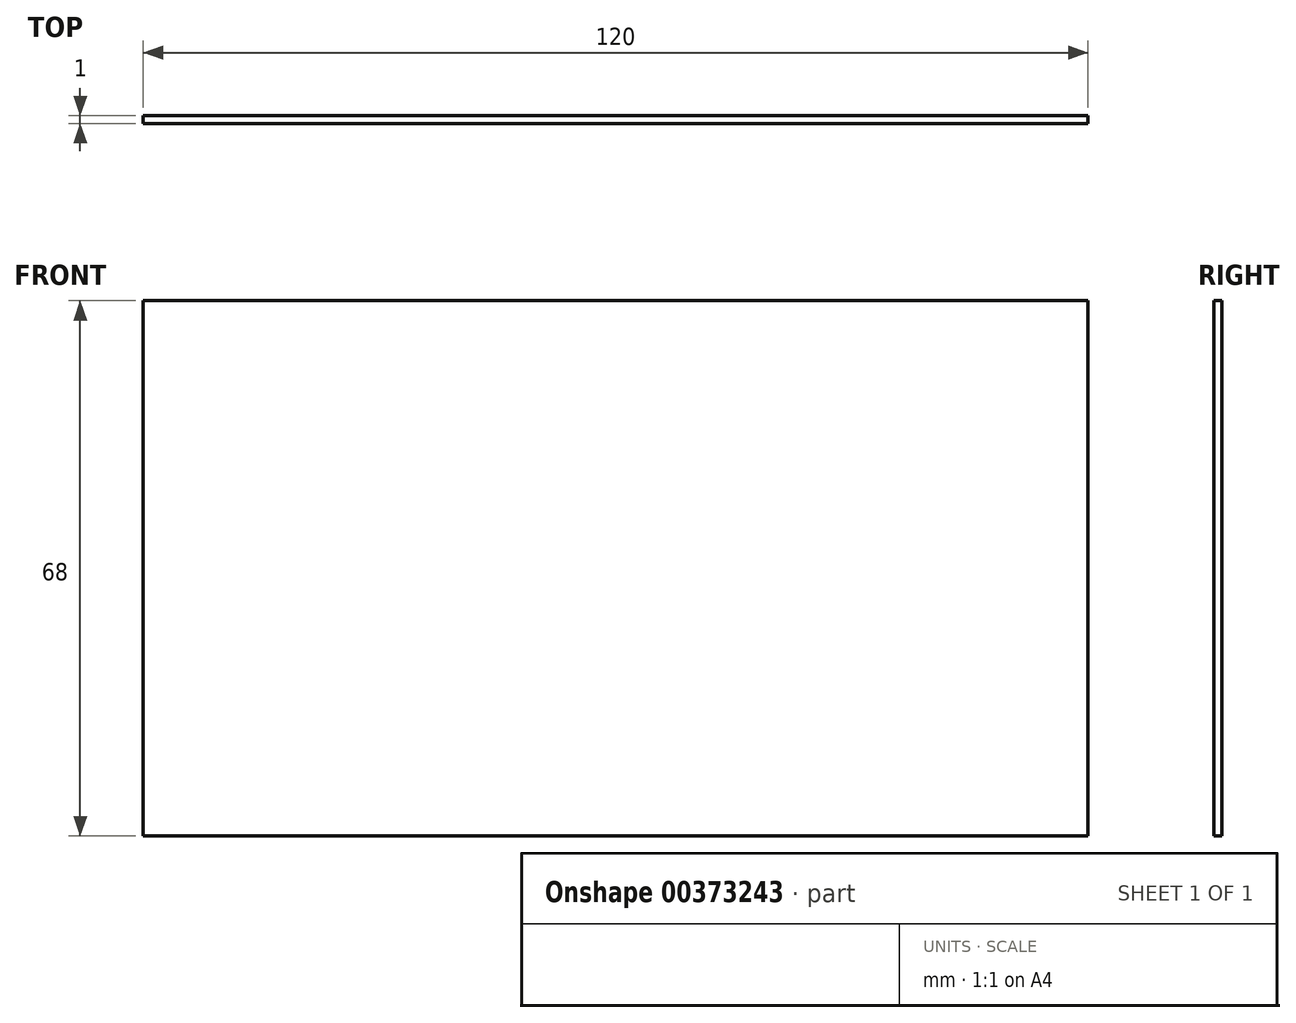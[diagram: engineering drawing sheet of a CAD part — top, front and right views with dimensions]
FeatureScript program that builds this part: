
annotation { "Feature Type Name" : "Feature", "Feature Type Description" : "" }
export const myFeature = defineFeature(function(context is Context, id is Id, definition is map)
    precondition{}
    {
        {
            var Q0;
            Q0=qCreatedBy(makeId("Front.planeOp"),FACE);
            var sketch = newSketch(context, id + "F0", { "sketchPlane" : qUnion([Q0])});
            skLineSegment(sketch, "E0.bottom", {"start": v(-67.48, 32.67) * mm, "end": v(52.52, 32.67) * mm});
            skLineSegment(sketch, "E0.top", {"start": v(-67.48, -35.33) * mm, "end": v(52.52, -35.33) * mm});
            skLineSegment(sketch, "E0.left", {"start": v(-67.48, 32.67) * mm, "end": v(-67.48, -35.33) * mm});
            skLineSegment(sketch, "E0.right", {"start": v(52.52, 32.67) * mm, "end": v(52.52, -35.33) * mm});
            skSolve(sketch);
        }
        {
            var Q0;
            Q0=qSketchRegion(id+"F0",true);
            extrude(context, id + "F1", {"entities" : qUnion([Q0]), "depth" : 1 * mm});
        }
    });
